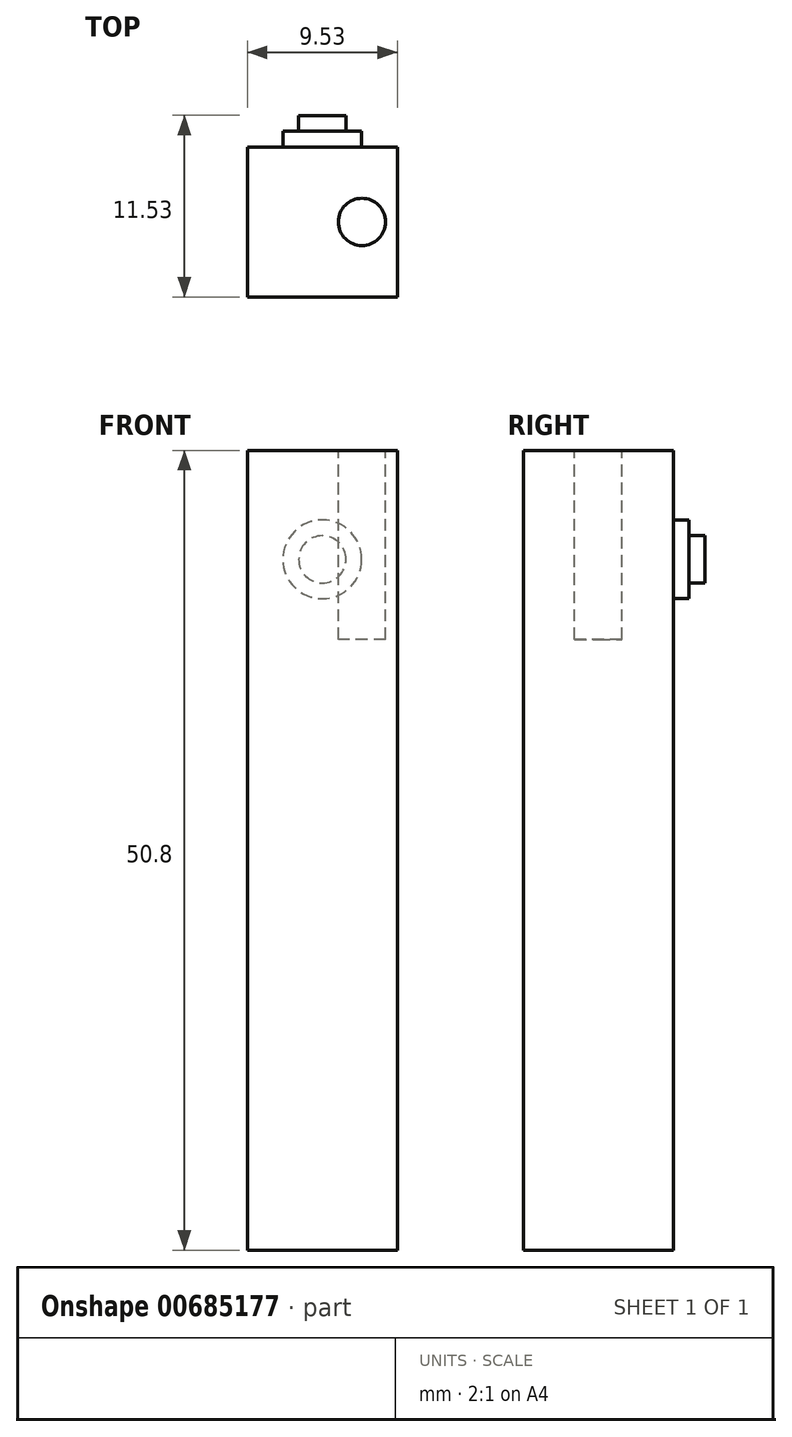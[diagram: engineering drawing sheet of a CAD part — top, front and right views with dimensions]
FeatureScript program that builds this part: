
annotation { "Feature Type Name" : "Feature", "Feature Type Description" : "" }
export const myFeature = defineFeature(function(context is Context, id is Id, definition is map)
    precondition{}
    {
        {
            var Q0;
            Q0=qCreatedBy(makeId("Top.planeOp"),FACE);
            var sketch = newSketch(context, id + "F0", { "sketchPlane" : qUnion([Q0])});
            skLineSegment(sketch, "E0.bottom", {"start": v(0, 0) * mm, "end": v(9.53, 0) * mm});
            skLineSegment(sketch, "E0.top", {"start": v(0, 9.53) * mm, "end": v(9.53, 9.53) * mm});
            skLineSegment(sketch, "E0.left", {"start": v(0, 0) * mm, "end": v(0, 9.53) * mm});
            skLineSegment(sketch, "E0.right", {"start": v(9.53, 0) * mm, "end": v(9.53, 9.53) * mm});
            skSolve(sketch);
        }
        {
            var Q0;
            Q0=qSketchRegion(id+"F0",true);
            extrude(context, id + "F1", {"entities" : qUnion([Q0]), "depth" : 50.8 * mm, "offsetDistance" : 25 * mm});
        }
        {
            var Q0;
            Q0=makeQuery(id+"F1.opExtrude","SWEPT_FACE",FACE,{"disambiguationData":[OSD([sQuery(id+"F0.wireOp",EDGE,"E0.top")])]});
            var sketch = newSketch(context, id + "F2", { "sketchPlane" : qUnion([Q0])});
            skCircle(sketch, "E1", {"center": v(-4.76, 43.88) * mm, "radius": 1.5 * mm});
            skLineSegment(sketch, "E2", {"start": v(0, 43.88) * mm, "end": v(-9.53, 43.88) * mm, "construction": true});
            skSolve(sketch);
        }
        {
            var Q0;
            Q0=qSketchRegion(id+"F2",true);
            var Q1;
            Q1=makeQuery(id+"F1.opExtrude","SWEPT_FACE",FACE,{"disambiguationData":[OSD([sQuery(id+"F0.wireOp",EDGE,"E0.bottom")])]});
            extrude(context, id + "F3", {"entities" : qUnion([Q0]), "endBound" : BoundingType.UP_TO_SURFACE, "oppositeDirection" : true, "depth" : 25 * mm, "endBoundEntityFace" : qUnion([Q1]), "offsetDistance" : 25 * mm});
        }
        {
            var Q0;
            Q0=makeQuery(id+"F3.opExtrude","CAP_FACE",FACE,{"disambiguationData":[OSD([sQuery(id+"F2.wireOp",EDGE,"E1")])],"isStart":true});
            var sketch = newSketch(context, id + "F4", { "sketchPlane" : qUnion([Q0])});
            skCircle(sketch, "E3", {"center": v(-4.76, 43.88) * mm, "radius": 2.5 * mm});
            skSolve(sketch);
        }
        {
            var Q0;
            Q0=qSketchRegion(id+"F4",true);
            extrude(context, id + "F5", {"entities" : qUnion([Q0]), "operationType" : NewBodyOperationType.ADD, "depth" : 1 * mm, "offsetDistance" : 25 * mm});
        }
        {
            var Q0;
            Q0=makeQuery(id+"F5.opExtrude","CAP_FACE",FACE,{"disambiguationData":[OSD([sQuery(id+"F4.wireOp",EDGE,"E3")])],"isStart":false});
            var sketch = newSketch(context, id + "F6", { "sketchPlane" : qUnion([Q0])});
            skCircle(sketch, "E4", {"center": v(-4.76, 43.88) * mm, "radius": 1.5 * mm});
            skSolve(sketch);
        }
        {
            var Q0;
            Q0=qSketchRegion(id+"F6",true);
            extrude(context, id + "F7", {"entities" : qUnion([Q0]), "operationType" : NewBodyOperationType.ADD, "depth" : 1 * mm, "offsetDistance" : 25 * mm});
        }
        {
            var Q0;
            Q0=makeQuery(id+"F1.opExtrude","CAP_FACE",FACE,{"disambiguationData":[OSD([sQuery(id+"F0.wireOp",EDGE,"E0.bottom"),sQuery(id+"F0.wireOp",EDGE,"E0.top"),sQuery(id+"F0.wireOp",EDGE,"E0.left"),sQuery(id+"F0.wireOp",EDGE,"E0.right")])],"isStart":false});
            var sketch = newSketch(context, id + "F8", { "sketchPlane" : qUnion([Q0])});
            skCircle(sketch, "E5", {"center": v(7.28, 4.76) * mm, "radius": 1.5 * mm});
            skLineSegment(sketch, "E6", {"start": v(7.28, 9.52) * mm, "end": v(7.28, 0) * mm, "construction": true});
            skSolve(sketch);
        }
        {
            var Q0;
            Q0=qSketchRegion(id+"F8",true);
            extrude(context, id + "F9", {"entities" : qUnion([Q0]), "oppositeDirection" : true, "depth" : 12 * mm, "offsetDistance" : 25 * mm});
        }
    });
